# Revit family: PROOX Behind-the-mirror paper towel dispenser X-Large EN
name_source: partatom
category: Furniture
revit_build: Autodesk Revit 2014 (Build: 20130308_1515(x64)
units: mm (PartAtom-declared; Revit-internal decimal feet)

## types (1)
- ZERO
    BIM objects producer = www.BIMtelligent.eu
    Cost = 145 $
    Default Elevation = 0 mm  [stored 0 ft]
    Description = Paper-towel dispenser for mounting behind the mirror XL
    EAN-No. = 9120050351325
    Manufacturer = PROOX Ltd.
    Material = PROOX stainless steel satin finish
    Model = ZE-111-XL
    Product data sheet = http://www.proox.com
    Specification = Paper towel dispenser in stainless steel with Teflon® coating for behind-the-mirror fitting.The dispenser is designed with 2 paper brakes and fully formed withdrawal lip for extremely easy sheet by sheet removal. Capacity approx. 450 - 600 towels. Suitable for paper towels with a length of approx. 215-250mm and a folded width of approx. 95-120 mm. The dispenser can be attached directly to the wall or to the lift module ZE-117
    Type Comments = ZERO
    URL = http://www.proox.com

note: [stored X ft] marks values corroborated as IEEE doubles in the binary element streams (Revit-internal decimal feet)

## geometry (parser evidence)
native form markers: Blend x18, Sweep x1
no freeform markers — native parametric forms only
